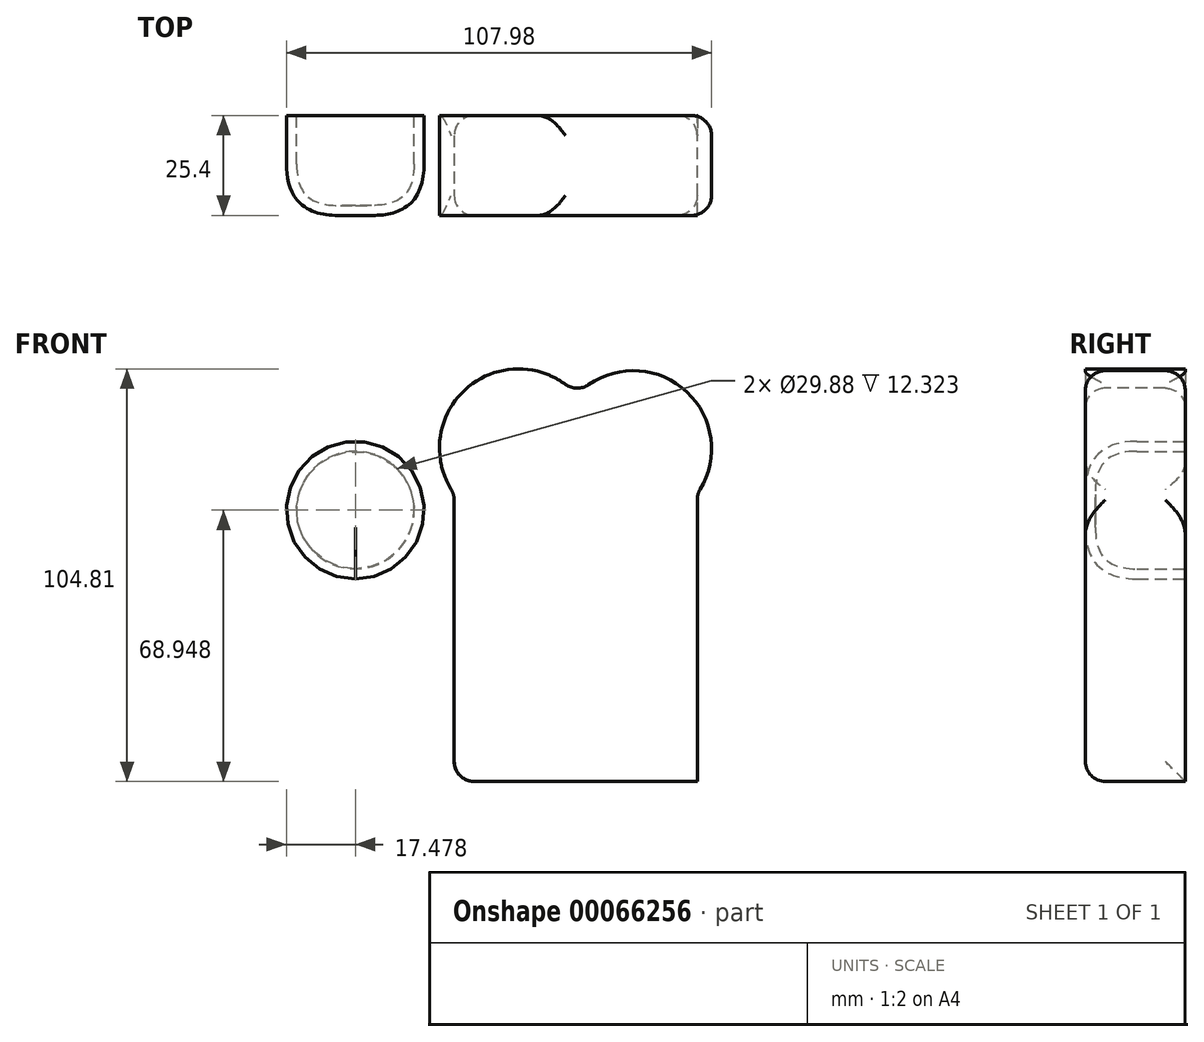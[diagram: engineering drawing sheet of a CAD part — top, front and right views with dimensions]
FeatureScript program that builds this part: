
annotation { "Feature Type Name" : "Feature", "Feature Type Description" : "" }
export const myFeature = defineFeature(function(context is Context, id is Id, definition is map)
    precondition{}
    {
        {
            var Q0;
            Q0=qCreatedBy(makeId("Front.planeOp"),FACE);
            var sketch = newSketch(context, id + "F0", { "sketchPlane" : qUnion([Q0])});
            skLineSegment(sketch, "E0.bottom", {"start": v(-31.16, 31.02) * mm, "end": v(30.58, 31.02) * mm});
            skLineSegment(sketch, "E0.top", {"start": v(-31.16, -42.03) * mm, "end": v(30.58, -42.03) * mm});
            skLineSegment(sketch, "E0.left", {"start": v(-31.16, 31.02) * mm, "end": v(-31.16, -42.03) * mm});
            skLineSegment(sketch, "E0.right", {"start": v(30.58, 31.02) * mm, "end": v(30.58, -42.03) * mm});
            skArc(sketch, "E1", {"start": v(0, 56.24) * mm, "mid": v(-27.46, 58.31) * mm, "end": v(-31.16, 31.02) * mm});
            skArc(sketch, "E2", {"start": v(30.58, 31.02) * mm, "mid": v(26.98, 57.8) * mm, "end": v(0, 56.24) * mm});
            skSolve(sketch);
        }
        {
            var Q0;
            Q0=makeQuery(id+"F0.imprint","IMPRINT",FACE,{"disambiguationData":[TD([[makeQuery(id+"F0.imprint","IMPRINT",EDGE,{"derivedFrom":sQuery(id+"F0.wireOp",EDGE,"E0.bottom")}),-1.0]])]});
            var Q1;
            Q1=makeQuery(id+"F0.imprint","IMPRINT",FACE,{"disambiguationData":[TD([[makeQuery(id+"F0.imprint","IMPRINT",EDGE,{"derivedFrom":sQuery(id+"F0.wireOp",EDGE,"E0.bottom")}),1.0]])]});
            extrude(context, id + "F1", {"entities" : qUnion([Q0, Q1]), "endBound" : BoundingType.SYMMETRIC, "depth" : 25.4 * mm});
        }
        {
            var Q0;
            Q0=makeQuery(id+"F1.opExtrude","CAP_EDGE",EDGE,{"disambiguationData":[OSD([sQuery(id+"F0.wireOp",EDGE,"E0.top")])],"isStart":false});
            var Q1;
            Q1=makeQuery(id+"F1.opExtrude","SWEPT_EDGE",EDGE,{"disambiguationData":[OSD([sQuery(id+"F0.wireOp",EDGE,"E0.top"),sQuery(id+"F0.wireOp",EDGE,"E0.left")])]});
            var Q2;
            Q2=makeQuery(id+"F1.opExtrude","CAP_EDGE",EDGE,{"disambiguationData":[OSD([sQuery(id+"F0.wireOp",EDGE,"E0.left")])],"isStart":false});
            var Q3;
            Q3=makeQuery(id+"F1.opExtrude","CAP_EDGE",EDGE,{"disambiguationData":[OSD([sQuery(id+"F0.wireOp",EDGE,"E0.left")])],"isStart":true});
            var Q4;
            Q4=makeQuery(id+"F1.opExtrude","SWEPT_EDGE",EDGE,{"disambiguationData":[OSD([sQuery(id+"F0.wireOp",EDGE,"E0.bottom"),sQuery(id+"F0.wireOp",EDGE,"E0.left"),sQuery(id+"F0.wireOp",EDGE,"E1")])]});
            var Q5;
            Q5=makeQuery(id+"F1.opExtrude","SWEPT_FACE",FACE,{"disambiguationData":[OSD([sQuery(id+"F0.wireOp",EDGE,"E2")])]});
            fillet(context, id + "F2", {"entities" : qUnion([Q0, Q1, Q2, Q3, Q4, Q5]), "radius" : 5.08 * mm, "tangentPropagation" : true, "allowEdgeOverflow" : false});
        }
        {
            var Q0;
            Q0=qCreatedBy(makeId("Front.planeOp"),FACE);
            var sketch = newSketch(context, id + "F3", { "sketchPlane" : qUnion([Q0])});
            skCircle(sketch, "E3", {"center": v(-56.3, 26.92) * mm, "radius": 17.48 * mm});
            skSolve(sketch);
        }
        {
            var Q0;
            Q0=makeQuery(id+"F3.imprint","IMPRINT",FACE,{"disambiguationData":[TD([[makeQuery(id+"F3.imprint","IMPRINT",EDGE,{"derivedFrom":sQuery(id+"F3.wireOp",EDGE,"E3")}),1.0]])]});
            extrude(context, id + "F4", {"entities" : qUnion([Q0]), "endBound" : BoundingType.SYMMETRIC, "depth" : 25.4 * mm});
        }
        {
            var Q0;
            Q0=makeQuery(id+"F4.opExtrude","CAP_FACE",FACE,{"disambiguationData":[OSD([sQuery(id+"F3.wireOp",EDGE,"E3")])],"isStart":false});
            fillet(context, id + "F5", {"entities" : qUnion([Q0]), "radius" : 13.08 * mm, "tangentPropagation" : true, "rho" : 0.5, "crossSection" : FilletCrossSection.CONIC, "allowEdgeOverflow" : false});
        }
        {
            var Q0;
            Q0=makeQuery(id+"F4.opExtrude","CAP_FACE",FACE,{"disambiguationData":[OSD([sQuery(id+"F3.wireOp",EDGE,"E3")])],"isStart":true});
            shell(context, id + "F6", {"entities" : qUnion([Q0]), "thickness" : 2.54 * mm});
        }
    });
